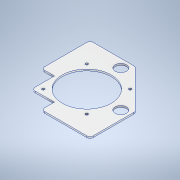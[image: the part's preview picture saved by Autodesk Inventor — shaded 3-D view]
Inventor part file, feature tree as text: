
AUTODESK INVENTOR PART (.ipt)
format: ipt  version: 2020 (Build 240168000, 168)  size: 185,344 bytes
history: native  units: in
note: dims shown in document units (in); Inventor stores cm internally (conversion verified against a paired STEP export)
features: sketch x4, extrude x3, hole x1, chamfer x1, fillet x1
ambient origin geometry x8: Origin, YZ Plane, XZ Plane, XY Plane, X Axis, Y Axis, Z Axis, Center Point
bodies: Solid1 (feature_tree)
feature tree (10):
  extrude  "Extrusion1"  Depth=0.125in TaperAngle=0.0deg
  hole  "Hole1"  [1 undecoded]
  extrude  "Extrusion3"  Depth=4.75in
  chamfer  "Chamfer1"  Distance=6.5in
  fillet  "Fillet4"  Radius=1.0in
  extrude  "Extrusion4"  Depth=2.75in
  sketch  "Sketch1"  dims[d0=3.8in d1=0.125in d2=0.0in]
  sketch  "Sketch2"  dims[d3=1.0in d4=1.0in]
  sketch  "Sketch4"  dims[d5=4.25in d9=4.75in]
  sketch  "Sketch5"  dims[d10=0.2031in d11=0.75in d12=0.5in d13=0.188in d14=0.5635in d15=1.0in d16=0.8108in d24=6.5in d26=1.0in d27=2.75in d28=1.75in d29=1.0in d30=0.0in d31=0.0in d33=3.0in d34=0.125in d35=45.0deg d36=0.25in d37=0.875in d38=5.454in d39=2.0in d40=1.8in d41=0.0in d42=0.0in]
note: 1 required parameter value undecoded (feature->parameter linkage not recoverable at this tier; creation-order binding heuristic only, values carry confidence <= 0.55)
